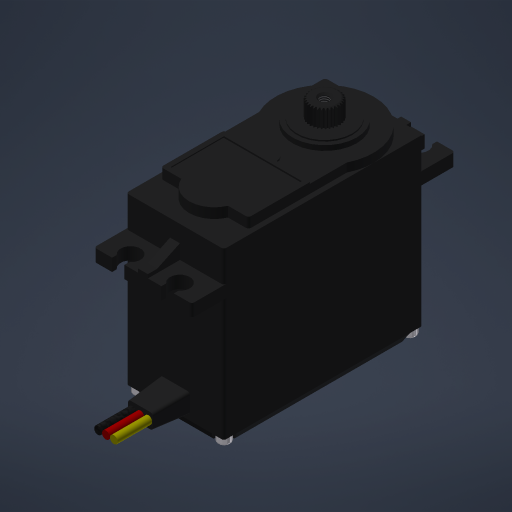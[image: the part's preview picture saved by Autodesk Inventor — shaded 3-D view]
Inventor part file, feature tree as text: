
AUTODESK INVENTOR PART (.ipt)
format: ipt  version: 2023 (Build 270158000, 158)  size: 724,992 bytes
history: native  units: mm
features: sketch x18, extrude x16, fillet x4, chamfer x2, other x2, plane x1, mirror x1, pattern_circular x1, thread x1, revolve x1, pattern_linear x1
ambient origin geometry x8: Origin, YZ Plane, XZ Plane, XY Plane, X Axis, Y Axis, Z Axis, Center Point
bodies: Solid1 (feature_tree)
feature tree (48):
  extrude  "Extrusion1"  Depth=9.9mm
  extrude  "Extrusion2"  Depth=35.25mm
  fillet  "Fillet1"  Radius=35.25mm
  extrude  "Extrusion3"  Depth=17.75mm
  plane  "Work Plane1"
  extrude  "Extrusion4"  Depth=8.875mm
  extrude  "Extrusion5"  Depth=1.966646mm
  mirror  "Mirror1"
  extrude  "Extrusion6"  Depth=1.75mm TaperAngle=0.0deg
  extrude  "Extrusion7"  Depth=12.8mm
  extrude  "Extrusion8"  Depth=0.5mm
  extrude  "Extrusion9"  Depth=1.0mm
  pattern_circular  "Circular Pattern1"  [2 undecoded]
  extrude  "Extrusion10"  Depth=0.5mm
  chamfer  "Chamfer1"  Distance=2.5mm
  thread  "Thread1"  [1 undecoded]
  revolve  "Revolution1"  [1 undecoded]
  chamfer  "Chamfer2"  Distance=27.036082mm
  fillet  "Fillet2"  Radius=2.0mm
  extrude  "Extrusion11"  Depth=13.0mm
  extrude  "Extrusion12"  Depth=1.0mm TaperAngle=0.0deg
  fillet  "Fillet3"  Radius=11.2mm
  extrude  "Extrusion13"  Depth=0.5mm TaperAngle=0.0deg
  pattern_linear  "Rectangular Pattern1"  Spacing1=5.8mm  [1 undecoded]
  extrude  "Extrusion14"  Depth=0.5mm
  fillet  "Fillet4"  Radius=3.6mm
  extrude  "Extrusion15"  Depth=0.4mm
  other  "Decal1"
  extrude  "Extrusion16"  Depth=0.5mm
  sketch  "Sketch1"  dims[d0=19.8mm d1=9.9mm]
  sketch  "Sketch2"  dims[d2=40.3mm d3=20.15mm d4=35.25mm d5=0.0mm]
  sketch  "Sketch3"  dims[d6=10.0mm d7=17.75mm]
  sketch  "Sketch4"  dims[d8=8.875mm d9=34.3mm]
  sketch  "Sketch5"  dims[d10=4.8mm d11=1.966646mm]
  sketch  "Sketch6"  dims[d12=10.249769mm d13=1.75mm d14=0.0mm]
  sketch  "Sketch7"  dims[d15=0.5mm d16=12.8mm]
  sketch  "Sketch8"  dims[d17=0.5mm d18=3.6mm]
  sketch  "Sketch9"  dims[d19=1.0mm d20=1.0mm]
  sketch  "Sketch10"  dims[d21=1.0mm]
  sketch  "Sketch11"  dims[d22=1.0mm]
  sketch  "Sketch12"  dims[d23=0.3mm d24=0.0mm]
  sketch  "Sketch13"  dims[d25=-8.8mm]
  sketch  "Sketch14"  dims[d26=6.5mm d27=6.5mm]
  sketch  "Sketch15"  dims[d28=4.0mm]
  sketch  "Sketch16"  dims[d29=2.5mm]
  sketch  "Sketch17"  dims[d31=5.0mm]
  other  "Image1"
  sketch  "Sketch18"  dims[d32=2.5mm d33=1.25mm d34=24.15mm d35=2.5mm d36=0.0mm d37=1.85575mm d38=0.740982mm d39=27.036082mm d40=2.0mm d41=0.0mm d42=13.0mm d43=1.0mm d44=0.0mm d45=11.2mm d46=0.26mm d47=0.0mm d48=5.8mm d49=5.2mm d50=3.6mm d51=0.0mm d52=0.4mm d53=4.363323mm d54=3.6mm d55=0.0mm d56=300.0mm d57=360.0deg d59=0.189756mm d60=0.189756mm d61=1.9mm d62=3.0mm d63=0.0mm d64=0.3mm d65=2.0mm d66=45.0deg d67=10.0mm d68=0.0mm d69=90.0deg d70=1.0mm d71=2.0mm d72=60.0deg d73=0.5mm d74=3.6mm d75=8.6mm d76=18.8mm d77=1.7mm d78=0.0mm d79=1.5mm d80=0.0mm d81=0.5mm d82=0.2mm d83=0.2mm d84=0.9mm d85=0.9mm d86=0.7mm d87=0.0mm d88=20.0mm d90=17.1mm d91=20.0mm d93=37.6mm d94=4.0mm d95=6.0mm d96=3.0mm d97=1.0mm d98=7.0mm d99=-0.698132mm d100=0.5mm d101=1.6mm d102=1.6mm d103=1.6mm d104=1.6mm d105=1.6mm d106=7.0mm d107=0.0mm d111=0.1mm d112=0.0mm d113=0.5mm d114=0.872665mm]
note: 5 required parameter values undecoded (feature->parameter linkage not recoverable at this tier; creation-order binding heuristic only, values carry confidence <= 0.55)